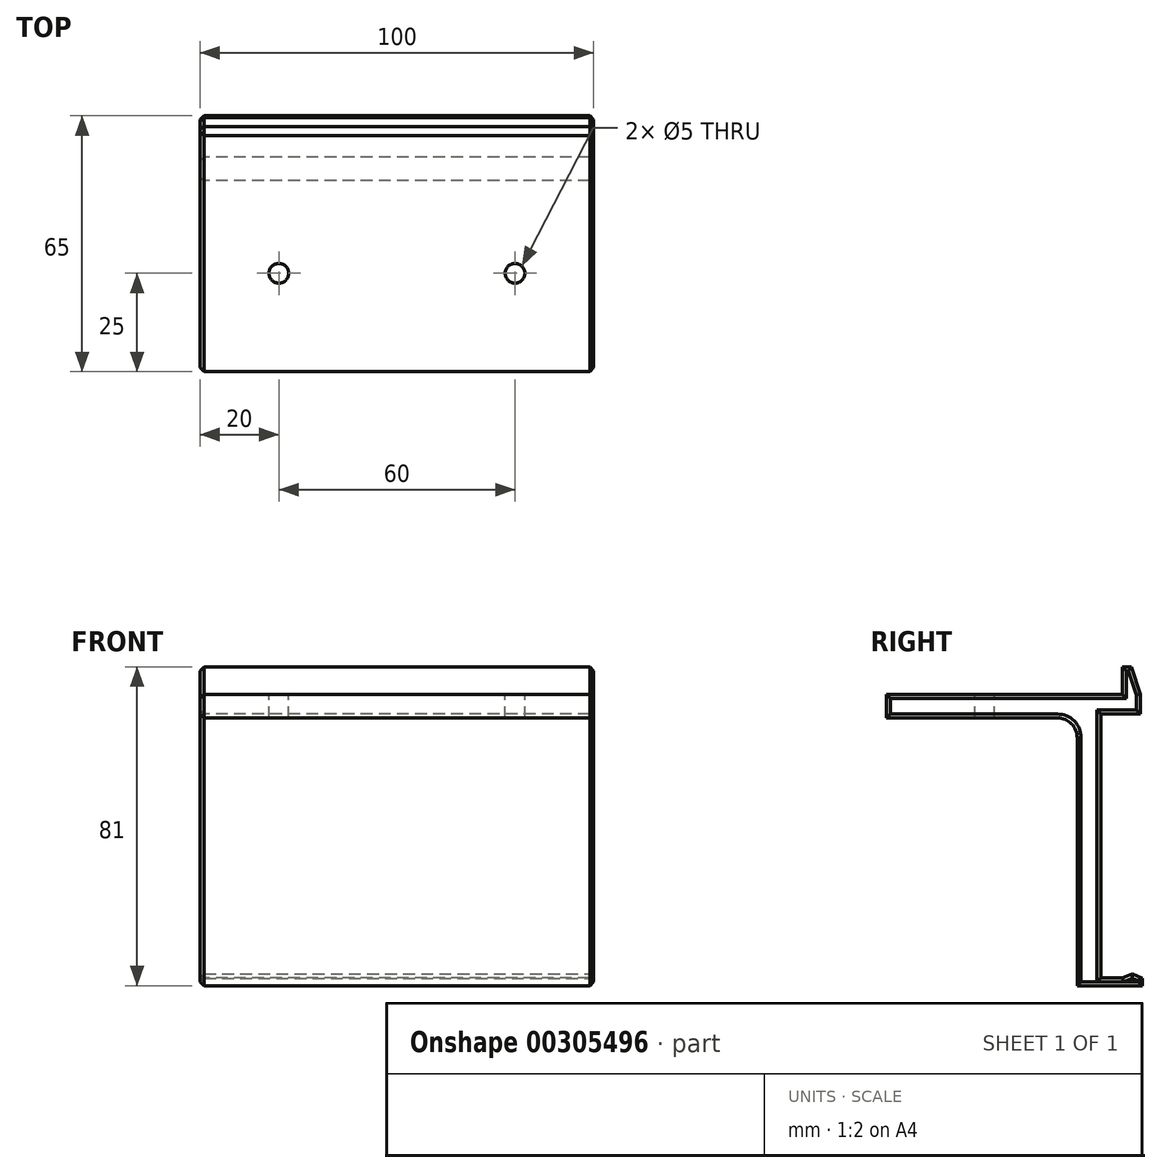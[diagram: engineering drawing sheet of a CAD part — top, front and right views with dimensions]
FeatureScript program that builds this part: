
annotation { "Feature Type Name" : "Feature", "Feature Type Description" : "" }
export const myFeature = defineFeature(function(context is Context, id is Id, definition is map)
    precondition{}
    {
        {
            var Q0;
            Q0=qCreatedBy(makeId("Right.planeOp"),FACE);
            var sketch = newSketch(context, id + "F0", { "sketchPlane" : qUnion([Q0])});
            skLineSegment(sketch, "E0", {"start": v(0, 0) * mm, "end": v(0, 7) * mm});
            skLineSegment(sketch, "E1", {"start": v(0, 7) * mm, "end": v(4.5, 7) * mm});
            skLineSegment(sketch, "E2", {"start": v(4.5, 7) * mm, "end": v(4.5, -5) * mm});
            skLineSegment(sketch, "E3", {"start": v(4.5, -5) * mm, "end": v(-5.5, -5) * mm});
            skLineSegment(sketch, "E4", {"start": v(-5.5, -5) * mm, "end": v(-5.5, -72) * mm});
            skLineSegment(sketch, "E5.MirrorCS", {"start": v(0, -72) * mm, "end": v(0, -71) * mm});
            skLineSegment(sketch, "E6.MirrorCS", {"start": v(5, -71) * mm, "end": v(5, -74) * mm});
            skLineSegment(sketch, "E7.MirrorCS", {"start": v(0, -71) * mm, "end": v(5, -71) * mm});
            skLineSegment(sketch, "E8.MirrorCS", {"start": v(-5.5, -72) * mm, "end": v(0, -72) * mm});
            skLineSegment(sketch, "E9", {"start": v(0, 0) * mm, "end": v(-60, 0) * mm});
            skLineSegment(sketch, "E10", {"start": v(-60, 0) * mm, "end": v(-60, -6) * mm});
            skLineSegment(sketch, "E11", {"start": v(-60, -6) * mm, "end": v(-11.5, -6) * mm});
            skLineSegment(sketch, "E12", {"start": v(5, -74) * mm, "end": v(-11.5, -74) * mm});
            skLineSegment(sketch, "E13", {"start": v(-11.5, -74) * mm, "end": v(-11.5, -6) * mm});
            skSolve(sketch);
        }
        {
            var Q0;
            Q0=makeQuery(id+"F0.imprint","IMPRINT",FACE,{"disambiguationData":[TD([[makeQuery(id+"F0.imprint","IMPRINT",EDGE,{"derivedFrom":sQuery(id+"F0.wireOp",EDGE,"E0")}),-1.0]])]});
            extrude(context, id + "F1", {"entities" : qUnion([Q0]), "endBound" : BoundingType.SYMMETRIC, "depth" : 100 * mm});
        }
        {
            var Q0;
            Q0=makeQuery(id+"F1.opExtrude","CAP_FACE",FACE,{"disambiguationData":[OSD([sQuery(id+"F0.wireOp",EDGE,"E0"),sQuery(id+"F0.wireOp",EDGE,"E1"),sQuery(id+"F0.wireOp",EDGE,"E2"),sQuery(id+"F0.wireOp",EDGE,"E3"),sQuery(id+"F0.wireOp",EDGE,"E4"),sQuery(id+"F0.wireOp",EDGE,"E5.MirrorCS"),sQuery(id+"F0.wireOp",EDGE,"E6.MirrorCS"),sQuery(id+"F0.wireOp",EDGE,"E7.MirrorCS"),sQuery(id+"F0.wireOp",EDGE,"E8.MirrorCS"),sQuery(id+"F0.wireOp",EDGE,"E9"),sQuery(id+"F0.wireOp",EDGE,"E10"),sQuery(id+"F0.wireOp",EDGE,"E11"),sQuery(id+"F0.wireOp",EDGE,"E12"),sQuery(id+"F0.wireOp",EDGE,"E13")])],"isStart":false});
            var sketch = newSketch(context, id + "F2", { "sketchPlane" : qUnion([Q0])});
            skLineSegment(sketch, "E14", {"start": v(2.25, 7) * mm, "end": v(4.5, 0) * mm});
            skPoint(sketch, "E14.endSnap0", {"position": v(4.5, 1) * mm});
            skLineSegment(sketch, "E15", {"start": v(4.5, 0) * mm, "end": v(4.5, 7) * mm});
            skLineSegment(sketch, "E16", {"start": v(4.5, 7) * mm, "end": v(2.25, 7) * mm});
            skSolve(sketch);
        }
        {
            var Q0;
            Q0=makeQuery(id+"F2.imprint","IMPRINT",FACE,{"disambiguationData":[TD([[makeQuery(id+"F2.imprint","IMPRINT",EDGE,{"derivedFrom":sQuery(id+"F2.wireOp",EDGE,"E14")}),1.0]])]});
            extrude(context, id + "F3", {"entities" : qUnion([Q0]), "operationType" : NewBodyOperationType.REMOVE, "endBound" : BoundingType.UP_TO_NEXT, "oppositeDirection" : true, "depth" : 25 * mm});
        }
        {
            var Q0;
            Q0=makeQuery(id+"F1.opExtrude","CAP_FACE",FACE,{"disambiguationData":[OSD([sQuery(id+"F0.wireOp",EDGE,"E0"),sQuery(id+"F0.wireOp",EDGE,"E1"),sQuery(id+"F0.wireOp",EDGE,"E2"),sQuery(id+"F0.wireOp",EDGE,"E3"),sQuery(id+"F0.wireOp",EDGE,"E4"),sQuery(id+"F0.wireOp",EDGE,"E5.MirrorCS"),sQuery(id+"F0.wireOp",EDGE,"E6.MirrorCS"),sQuery(id+"F0.wireOp",EDGE,"E7.MirrorCS"),sQuery(id+"F0.wireOp",EDGE,"E8.MirrorCS"),sQuery(id+"F0.wireOp",EDGE,"E9"),sQuery(id+"F0.wireOp",EDGE,"E10"),sQuery(id+"F0.wireOp",EDGE,"E11"),sQuery(id+"F0.wireOp",EDGE,"E12"),sQuery(id+"F0.wireOp",EDGE,"E13")])],"isStart":false});
            var sketch = newSketch(context, id + "F4", { "sketchPlane" : qUnion([Q0])});
            skLineSegment(sketch, "E17", {"start": v(0, -72) * mm, "end": v(2.5, -71) * mm});
            skLineSegment(sketch, "E18", {"start": v(2.5, -71) * mm, "end": v(0, -71) * mm});
            skLineSegment(sketch, "E19", {"start": v(0, -71) * mm, "end": v(0, -72) * mm});
            skLineSegment(sketch, "E20", {"start": v(2.5, -71) * mm, "end": v(5, -72.1) * mm});
            skLineSegment(sketch, "E21", {"start": v(5, -72.1) * mm, "end": v(5, -71) * mm});
            skLineSegment(sketch, "E22", {"start": v(2.5, -71) * mm, "end": v(5, -71) * mm});
            skSolve(sketch);
        }
        {
            var Q0;
            Q0=makeQuery(id+"F4.imprint","IMPRINT",FACE,{"disambiguationData":[TD([[makeQuery(id+"F4.imprint","IMPRINT",EDGE,{"derivedFrom":sQuery(id+"F4.wireOp",EDGE,"E17")}),1.0]])]});
            var Q1;
            Q1=makeQuery(id+"F4.imprint","IMPRINT",FACE,{"disambiguationData":[TD([[makeQuery(id+"F4.imprint","IMPRINT",EDGE,{"derivedFrom":sQuery(id+"F4.wireOp",EDGE,"E20")}),1.0]])]});
            extrude(context, id + "F5", {"entities" : qUnion([Q0, Q1]), "operationType" : NewBodyOperationType.REMOVE, "endBound" : BoundingType.UP_TO_NEXT, "oppositeDirection" : true, "depth" : 25 * mm});
        }
        {
            var Q0;
            Q0=makeQuery(id+"F1.opExtrude","SWEPT_FACE",FACE,{"disambiguationData":[OSD([sQuery(id+"F0.wireOp",EDGE,"E9")])]});
            var sketch = newSketch(context, id + "F6", { "sketchPlane" : qUnion([Q0])});
            skLineSegment(sketch, "E23", {"start": v(-50, -60) * mm, "end": v(-50, -35) * mm, "construction": true});
            skLineSegment(sketch, "E24", {"start": v(-50, -35) * mm, "end": v(-30, -35) * mm, "construction": true});
            skLineSegment(sketch, "E25", {"start": v(-30, -35) * mm, "end": v(30, -35) * mm, "construction": true});
            skCircle(sketch, "E26", {"center": v(-30, -35) * mm, "radius": 2.5 * mm});
            skCircle(sketch, "E27", {"center": v(30, -35) * mm, "radius": 2.5 * mm});
            skSolve(sketch);
        }
        {
            var Q0;
            Q0=makeQuery(id+"F6.imprint","IMPRINT",FACE,{"disambiguationData":[TD([[makeQuery(id+"F6.imprint","IMPRINT",EDGE,{"derivedFrom":sQuery(id+"F6.wireOp",EDGE,"E26")}),1.0]])]});
            var Q1;
            Q1=makeQuery(id+"F6.imprint","IMPRINT",FACE,{"disambiguationData":[TD([[makeQuery(id+"F6.imprint","IMPRINT",EDGE,{"derivedFrom":sQuery(id+"F6.wireOp",EDGE,"E27")}),1.0]])]});
            extrude(context, id + "F7", {"entities" : qUnion([Q0, Q1]), "operationType" : NewBodyOperationType.REMOVE, "endBound" : BoundingType.UP_TO_NEXT, "oppositeDirection" : true, "depth" : 25 * mm});
        }
        {
            var Q0;
            Q0=makeQuery(id+"F1.opExtrude","SWEPT_EDGE",EDGE,{"disambiguationData":[OSD([sQuery(id+"F0.wireOp",EDGE,"E11"),sQuery(id+"F0.wireOp",EDGE,"E13")])]});
            fillet(context, id + "F8", {"entities" : qUnion([Q0]), "radius" : 5 * mm, "tangentPropagation" : true, "allowEdgeOverflow" : false});
        }
        {
            var Q0;
            Q0=makeQuery(id+"F1.opExtrude","CAP_FACE",FACE,{"disambiguationData":[OSD([sQuery(id+"F0.wireOp",EDGE,"E0"),sQuery(id+"F0.wireOp",EDGE,"E1"),sQuery(id+"F0.wireOp",EDGE,"E2"),sQuery(id+"F0.wireOp",EDGE,"E3"),sQuery(id+"F0.wireOp",EDGE,"E4"),sQuery(id+"F0.wireOp",EDGE,"E5.MirrorCS"),sQuery(id+"F0.wireOp",EDGE,"E6.MirrorCS"),sQuery(id+"F0.wireOp",EDGE,"E7.MirrorCS"),sQuery(id+"F0.wireOp",EDGE,"E8.MirrorCS"),sQuery(id+"F0.wireOp",EDGE,"E9"),sQuery(id+"F0.wireOp",EDGE,"E10"),sQuery(id+"F0.wireOp",EDGE,"E11"),sQuery(id+"F0.wireOp",EDGE,"E12"),sQuery(id+"F0.wireOp",EDGE,"E13")])],"isStart":false});
            var Q1;
            Q1=makeQuery(id+"F1.opExtrude","CAP_FACE",FACE,{"disambiguationData":[OSD([sQuery(id+"F0.wireOp",EDGE,"E0"),sQuery(id+"F0.wireOp",EDGE,"E1"),sQuery(id+"F0.wireOp",EDGE,"E2"),sQuery(id+"F0.wireOp",EDGE,"E3"),sQuery(id+"F0.wireOp",EDGE,"E4"),sQuery(id+"F0.wireOp",EDGE,"E5.MirrorCS"),sQuery(id+"F0.wireOp",EDGE,"E6.MirrorCS"),sQuery(id+"F0.wireOp",EDGE,"E7.MirrorCS"),sQuery(id+"F0.wireOp",EDGE,"E8.MirrorCS"),sQuery(id+"F0.wireOp",EDGE,"E9"),sQuery(id+"F0.wireOp",EDGE,"E10"),sQuery(id+"F0.wireOp",EDGE,"E11"),sQuery(id+"F0.wireOp",EDGE,"E12"),sQuery(id+"F0.wireOp",EDGE,"E13")])],"isStart":true});
            chamfer(context, id + "F9", {"entities" : qUnion([Q0, Q1]), "width" : 1 * mm, "tangentPropagation" : true});
        }
    });
